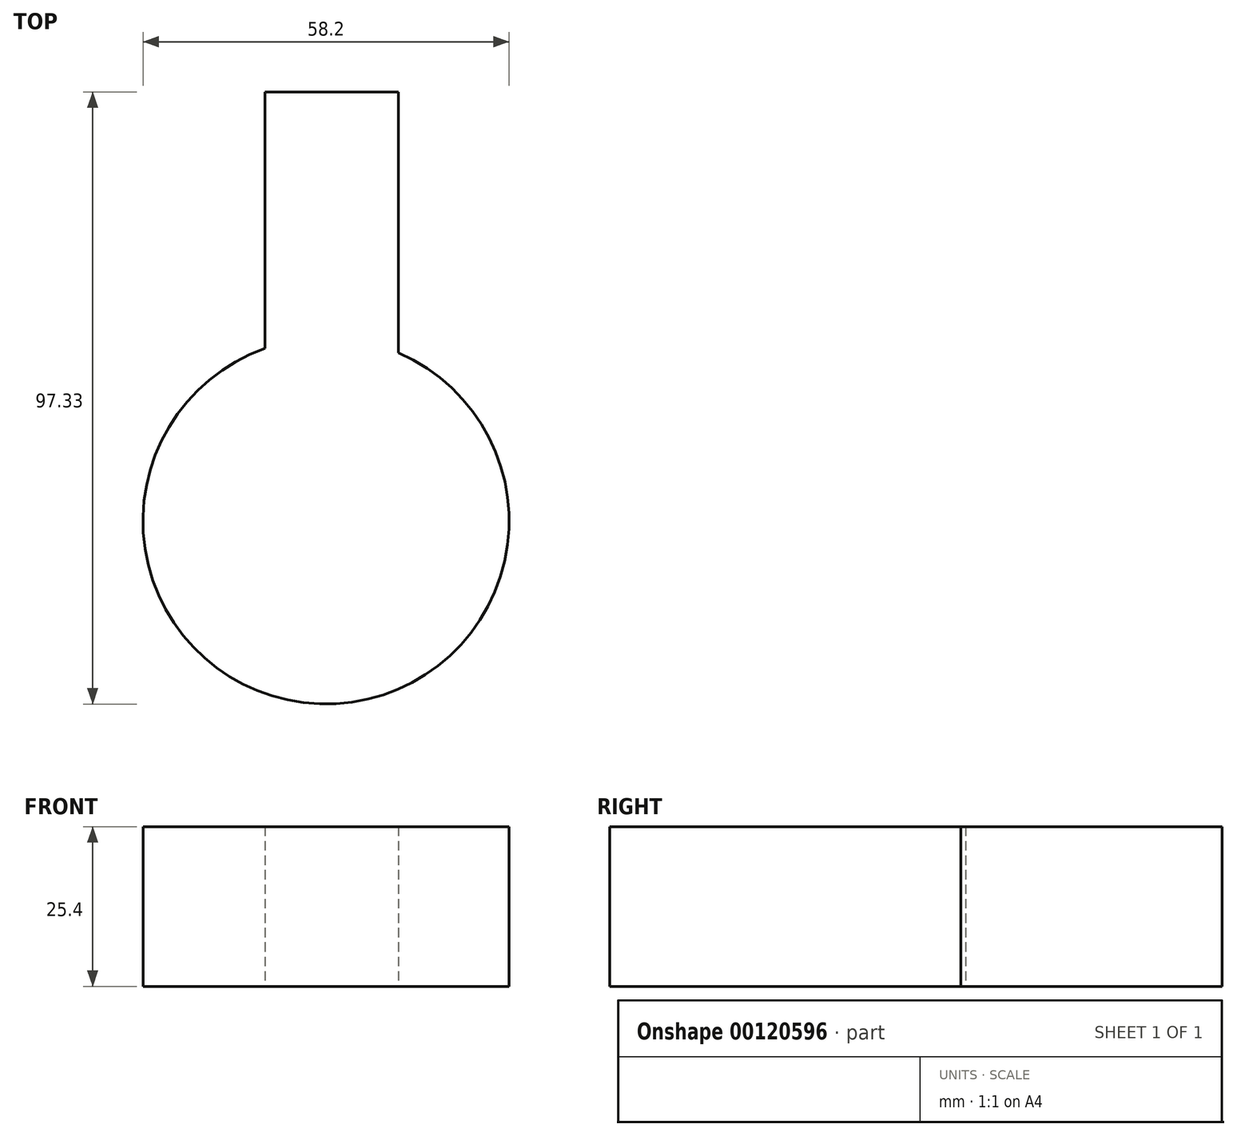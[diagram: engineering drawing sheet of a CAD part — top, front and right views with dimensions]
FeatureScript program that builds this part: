
annotation { "Feature Type Name" : "Feature", "Feature Type Description" : "" }
export const myFeature = defineFeature(function(context is Context, id is Id, definition is map)
    precondition{}
    {
        {
            var Q0;
            Q0=qCreatedBy(makeId("Top.planeOp"),FACE);
            var sketch = newSketch(context, id + "F0", { "sketchPlane" : qUnion([Q0])});
            skArc(sketch, "E0", {"start": v(-9.68, 27.44) * mm, "mid": v(-0.99, -29.08) * mm, "end": v(11.52, 26.72) * mm});
            skLineSegment(sketch, "E1", {"start": v(-9.68, 27.44) * mm, "end": v(-9.68, 68.23) * mm});
            skLineSegment(sketch, "E2", {"start": v(-9.68, 68.23) * mm, "end": v(11.52, 68.23) * mm});
            skLineSegment(sketch, "E3", {"start": v(11.52, 68.23) * mm, "end": v(11.52, 26.72) * mm});
            skSolve(sketch);
        }
        {
            var Q0;
            Q0=makeQuery(id+"F0.imprint","IMPRINT",FACE,{"disambiguationData":[TD([[makeQuery(id+"F0.imprint","IMPRINT",EDGE,{"derivedFrom":sQuery(id+"F0.wireOp",EDGE,"E0")}),1.0]])]});
            extrude(context, id + "F1", {"entities" : qUnion([Q0]), "depth" : 25.4 * mm});
        }
    });
